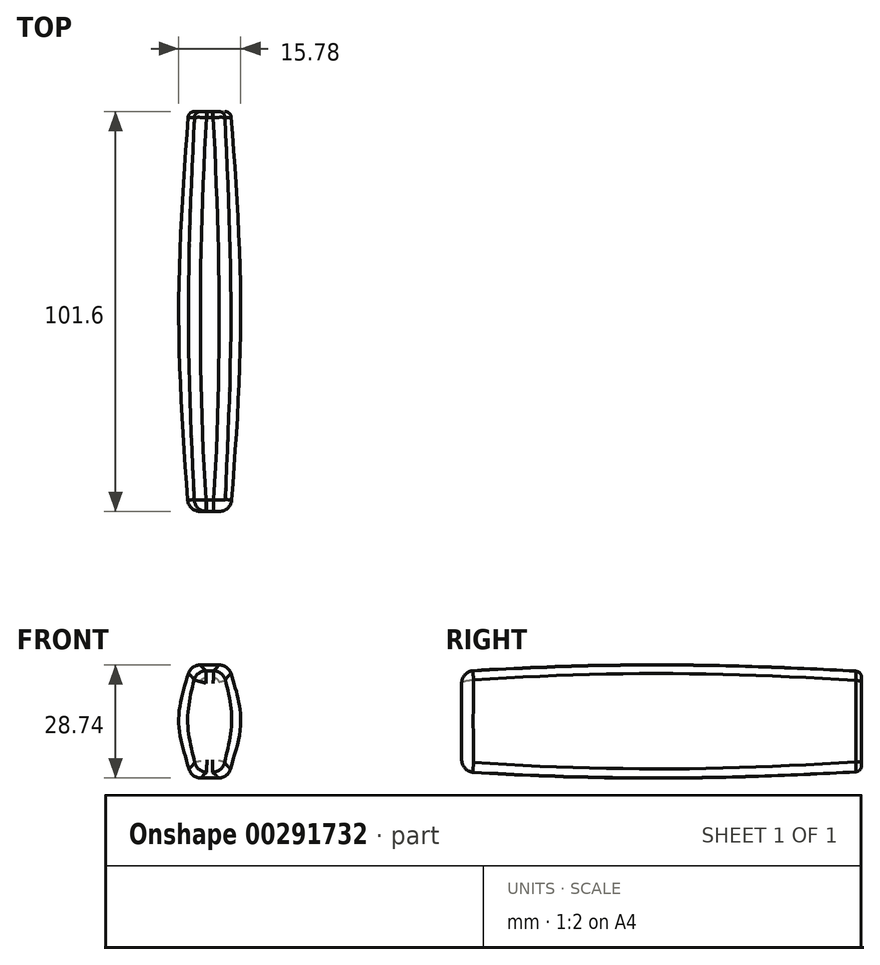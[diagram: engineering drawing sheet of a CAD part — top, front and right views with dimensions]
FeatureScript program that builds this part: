
annotation { "Feature Type Name" : "Feature", "Feature Type Description" : "" }
export const myFeature = defineFeature(function(context is Context, id is Id, definition is map)
    precondition{}
    {
        {
            var Q0;
            Q0=qCreatedBy(makeId("Front.planeOp"),FACE);
            var sketch = newSketch(context, id + "F0", { "sketchPlane" : qUnion([Q0])});
            skLineSegment(sketch, "E0.bottom", {"start": v(3.18, -12.7) * mm, "end": v(-3.18, -12.7) * mm});
            skLineSegment(sketch, "E0.top", {"start": v(3.18, 12.7) * mm, "end": v(-3.18, 12.7) * mm});
            skPoint(sketch, "E0.middle", {"position": v(0, 0) * mm});
            skFitSpline(sketch, "E1", {"points": [v(-3.18, 12.7) * mm, v(-5.38, 0) * mm, v(-3.18, -12.7) * mm, v(0, -43.12) * mm], "startDerivative": vector(-12, -40.51) * mm, "endDerivative": vector(6.2, -72.56) * mm});
            skFitSpline(sketch, "E2.MirrorCS", {"points": [v(3.18, 12.7) * mm, v(5.38, 0) * mm, v(3.18, -12.7) * mm, v(0, -43.12) * mm], "startDerivative": vector(12, -40.51) * mm, "endDerivative": vector(-6.2, -72.56) * mm});
            skSolve(sketch);
        }
        {
            var Q0;
            Q0=qCreatedBy(makeId("Front.planeOp"),FACE);
            cPlane(context, id + "F1", {"entities" : qUnion([Q0]), "cplaneType" : CPlaneType.OFFSET, "offset" : 50.8 * mm, "oppositeDirection" : true, "width" : 152.4 * mm, "height" : 152.4 * mm});
        }
        {
            var Q0;
            Q0=qCreatedBy(id+"F1.planeOp",FACE);
            var sketch = newSketch(context, id + "F2", { "sketchPlane" : qUnion([Q0])});
            skLineSegment(sketch, "E3.bottom", {"start": v(4.67, -14.37) * mm, "end": v(-4.67, -14.37) * mm});
            skLineSegment(sketch, "E3.top", {"start": v(4.67, 14.37) * mm, "end": v(-4.67, 14.37) * mm});
            skPoint(sketch, "E3.middle", {"position": v(0, 0) * mm});
            skFitSpline(sketch, "E4", {"points": [v(-4.67, 14.37) * mm, v(-7.89, 0) * mm, v(-4.67, -14.37) * mm, v(0, -43.12) * mm], "startDerivative": vector(-16.64, -49.82) * mm, "endDerivative": vector(9.86, -74.6) * mm});
            skFitSpline(sketch, "E5.MirrorCS", {"points": [v(4.67, 14.37) * mm, v(7.89, 0) * mm, v(4.67, -14.37) * mm, v(0, -43.12) * mm], "startDerivative": vector(16.64, -49.82) * mm, "endDerivative": vector(-9.86, -74.6) * mm});
            skSolve(sketch);
        }
        {
            var Q0;
            Q0=makeQuery(id+"F0.imprint","IMPRINT",FACE,{"disambiguationData":[TD([[makeQuery(id+"F0.imprint","IMPRINT",EDGE,{"derivedFrom":sQuery(id+"F0.wireOp",EDGE,"E0.bottom")}),-1.0]])]});
            var sketch = newSketch(context, id + "F3", { "sketchPlane" : qUnion([Q0])});
            skSolve(sketch);
        }
        {
            var Q0;
            Q0=qCreatedBy(id+"F1.planeOp",FACE);
            cPlane(context, id + "F4", {"entities" : qUnion([Q0]), "cplaneType" : CPlaneType.OFFSET, "offset" : 50.8 * mm, "oppositeDirection" : true, "width" : 152.4 * mm, "height" : 152.4 * mm});
        }
        {
            var Q0;
            Q0=qCreatedBy(id+"F4.planeOp",FACE);
            var sketch = newSketch(context, id + "F5", { "sketchPlane" : qUnion([Q0])});
            skLineSegment(sketch, "E6.bottom", {"start": v(3.17, -12.7) * mm, "end": v(-3.17, -12.7) * mm});
            skLineSegment(sketch, "E6.top", {"start": v(3.18, 12.7) * mm, "end": v(-3.17, 12.7) * mm});
            skPoint(sketch, "E6.middle", {"position": v(0, 0) * mm});
            skFitSpline(sketch, "E7.MirrorCS", {"points": [v(3.17, 12.7) * mm, v(5.38, 0) * mm, v(3.17, -12.7) * mm, v(0, -43.12) * mm], "startDerivative": vector(12, -40.51) * mm, "endDerivative": vector(0, -59.95) * mm});
            skFitSpline(sketch, "E8.MirrorCS", {"points": [v(-3.17, 12.7) * mm, v(-5.38, 0) * mm, v(-3.17, -12.7) * mm, v(0, -43.12) * mm], "startDerivative": vector(-12, -40.51) * mm, "endDerivative": vector(0, -59.95) * mm});
            skSolve(sketch);
        }
        {
            var Q0;
            Q0=qCreatedBy(makeId("Right.planeOp"),FACE);
            var sketch = newSketch(context, id + "F6", { "sketchPlane" : qUnion([Q0])});
            skFitSpline(sketch, "E9", {"points": [v(0, 12.7) * mm, v(50.8, 14.37) * mm, v(101.6, 12.7) * mm], "startDerivative": vector(101.7, 7.24) * mm, "endDerivative": vector(101.7, -6.04) * mm});
            skFitSpline(sketch, "E10.MirrorCS", {"points": [v(0, -12.7) * mm, v(50.8, -14.37) * mm, v(101.6, -12.7) * mm], "startDerivative": vector(101.7, -7.24) * mm, "endDerivative": vector(101.7, 6.04) * mm});
            skSolve(sketch);
        }
        {
            var Q0;
            Q0=makeQuery(id+"F5.imprint","IMPRINT",FACE,{"disambiguationData":[TD([[makeQuery(id+"F5.imprint","IMPRINT",EDGE,{"derivedFrom":sQuery(id+"F5.wireOp",EDGE,"E6.bottom")}),-1.0]])]});
            var Q1;
            Q1=makeQuery(id+"F2.imprint","IMPRINT",FACE,{"disambiguationData":[TD([[makeQuery(id+"F2.imprint","IMPRINT",EDGE,{"derivedFrom":sQuery(id+"F2.wireOp",EDGE,"E3.bottom")}),-1.0]])]});
            var Q2;
            Q2=makeQuery(id+"F3.imprint","IMPRINT",FACE,{"disambiguationData":[TD([[makeQuery(id+"F3.imprint","IMPRINT",EDGE,{"derivedFrom":makeQuery(id+"F0.imprint","IMPRINT",EDGE,{"derivedFrom":sQuery(id+"F0.wireOp",EDGE,"E0.bottom")})}),-1.0]])]});
            var Q3;
            Q3=makeQuery(id+"F5.imprint","IMPRINT",FACE,{"disambiguationData":[TD([[makeQuery(id+"F5.imprint","IMPRINT",EDGE,{"derivedFrom":sQuery(id+"F5.wireOp",EDGE,"E6.bottom")}),-1.0]])]});
            var Q4;
            Q4=makeQuery(id+"F2.imprint","IMPRINT",FACE,{"disambiguationData":[TD([[makeQuery(id+"F2.imprint","IMPRINT",EDGE,{"derivedFrom":sQuery(id+"F2.wireOp",EDGE,"E3.bottom")}),-1.0]])]});
            var Q5;
            Q5=makeQuery(id+"F3.imprint","IMPRINT",FACE,{"disambiguationData":[TD([[makeQuery(id+"F3.imprint","IMPRINT",EDGE,{"derivedFrom":makeQuery(id+"F0.imprint","IMPRINT",EDGE,{"derivedFrom":sQuery(id+"F0.wireOp",EDGE,"E0.bottom")})}),-1.0]])]});
            var Q6;
            Q6=sQuery(id+"F6.wireOp",EDGE,"E9");
            var Q7;
            Q7=sQuery(id+"F6.wireOp",EDGE,"E10.MirrorCS");
            loft(context, id + "F7", {"addGuides" : true, "sheetProfilesArray" : [{ "sheetProfileEntities" : qUnion([Q0]) }, { "sheetProfileEntities" : qUnion([Q1]) }, { "sheetProfileEntities" : qUnion([Q2]) }], "wireProfilesArray" : [{ "wireProfileEntities" : qUnion([Q3]) }, { "wireProfileEntities" : qUnion([Q4]) }, { "wireProfileEntities" : qUnion([Q5]) }], "guidesArray" : [{ "guideEntities" : qUnion([Q6]), "guideDerivativeType" : LoftGuideDerivativeType.DEFAULT, "guideDerivativeMagnitude" : 1 }, { "guideEntities" : qUnion([Q7]), "guideDerivativeType" : LoftGuideDerivativeType.DEFAULT, "guideDerivativeMagnitude" : 1 }]});
        }
        {
            var Q0;
            Q0=makeQuery(id+"F7.opLoft","SWEPT_EDGE",EDGE,{"disambiguationData":[OSD([sQuery(id+"F2.wireOp",EDGE,"E3.top"),sQuery(id+"F2.wireOp",EDGE,"E5.MirrorCS"),sQuery(id+"F5.wireOp",EDGE,"E6.top"),sQuery(id+"F5.wireOp",EDGE,"E7.MirrorCS")])]});
            var Q1;
            Q1=makeQuery(id+"F7.opLoft","SWEPT_EDGE",EDGE,{"disambiguationData":[OSD([sQuery(id+"F2.wireOp",EDGE,"E3.top"),sQuery(id+"F2.wireOp",EDGE,"E4"),sQuery(id+"F5.wireOp",EDGE,"E6.top"),sQuery(id+"F5.wireOp",EDGE,"E8.MirrorCS")])]});
            var Q2;
            Q2=makeQuery(id+"F7.opLoft","SWEPT_EDGE",EDGE,{"disambiguationData":[OSD([sQuery(id+"F2.wireOp",EDGE,"E3.bottom"),sQuery(id+"F2.wireOp",EDGE,"E4"),sQuery(id+"F5.wireOp",EDGE,"E6.bottom"),sQuery(id+"F5.wireOp",EDGE,"E8.MirrorCS")])]});
            var Q3;
            Q3=makeQuery(id+"F7.opLoft","SWEPT_EDGE",EDGE,{"disambiguationData":[OSD([sQuery(id+"F2.wireOp",EDGE,"E3.bottom"),sQuery(id+"F2.wireOp",EDGE,"E5.MirrorCS"),sQuery(id+"F5.wireOp",EDGE,"E6.bottom"),sQuery(id+"F5.wireOp",EDGE,"E7.MirrorCS")])]});
            fillet(context, id + "F8", {"entities" : qUnion([Q0, Q1, Q2, Q3]), "radius" : 3.17 * mm, "tangentPropagation" : true, "allowEdgeOverflow" : false});
        }
        {
            var Q0;
            Q0=makeQuery(id+"F7.opLoft","CAP_FACE",FACE,{"disambiguationData":[OSD([makeQuery(id+"F5.imprint","IMPRINT",FACE,{"disambiguationData":[TD([[makeQuery(id+"F5.imprint","IMPRINT",EDGE,{"derivedFrom":sQuery(id+"F5.wireOp",EDGE,"E6.bottom")}),-1.0]])]})])],"isStart":true});
            fillet(context, id + "F9", {"entities" : qUnion([Q0]), "radius" : 1.59 * mm, "tangentPropagation" : true, "allowEdgeOverflow" : false});
        }
        {
            var Q0;
            Q0=makeQuery(id+"F7.opLoft","CAP_FACE",FACE,{"disambiguationData":[OSD([makeQuery(id+"F3.imprint","IMPRINT",FACE,{"disambiguationData":[TD([[makeQuery(id+"F3.imprint","IMPRINT",EDGE,{"derivedFrom":makeQuery(id+"F0.imprint","IMPRINT",EDGE,{"derivedFrom":sQuery(id+"F0.wireOp",EDGE,"E0.bottom")})}),-1.0]])]})])],"isStart":true});
            fillet(context, id + "F10", {"entities" : qUnion([Q0]), "radius" : 3.17 * mm, "tangentPropagation" : true, "allowEdgeOverflow" : false});
        }
    });
